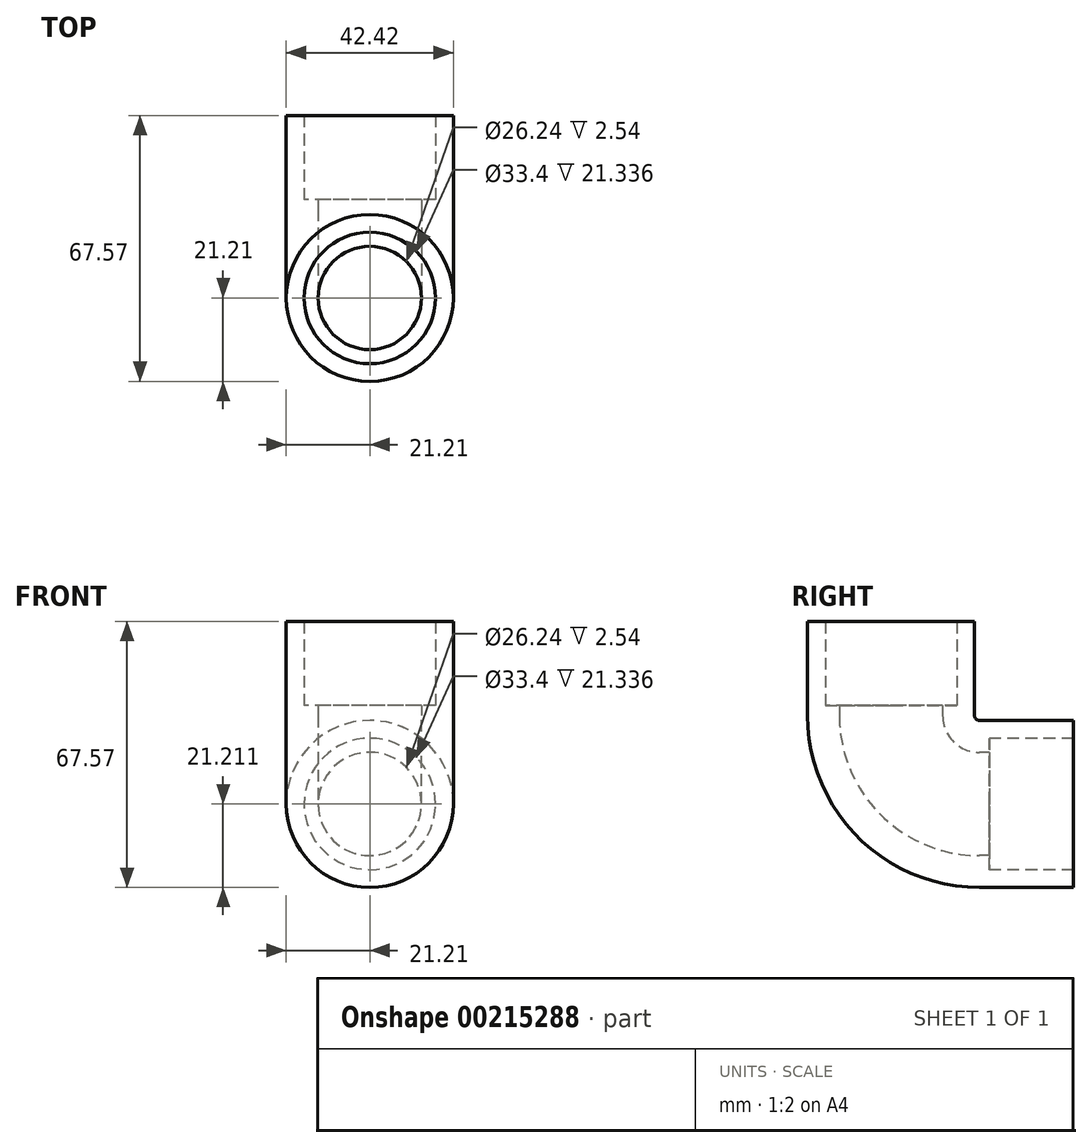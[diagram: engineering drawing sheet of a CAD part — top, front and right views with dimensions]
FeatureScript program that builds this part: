
annotation { "Feature Type Name" : "Feature", "Feature Type Description" : "" }
export const myFeature = defineFeature(function(context is Context, id is Id, definition is map)
    precondition{}
    {
        {
            var Q0;
            Q0=qCreatedBy(makeId("Top.planeOp"),FACE);
            var sketch = newSketch(context, id + "F0", { "sketchPlane" : qUnion([Q0])});
            skCircle(sketch, "E0", {"center": v(0, 0) * mm, "radius": 16.7 * mm});
            skCircle(sketch, "E1", {"center": v(0, 0) * mm, "radius": 13.12 * mm});
            skCircle(sketch, "E2", {"center": v(0, 0) * mm, "radius": 21.2 * mm});
            skSolve(sketch);
        }
        {
            var Q0;
            Q0=makeQuery(id+"F0.imprint","IMPRINT",FACE,{"disambiguationData":[TD([[makeQuery(id+"F0.imprint","IMPRINT",EDGE,{"derivedFrom":sQuery(id+"F0.wireOp",EDGE,"E0")}),1.0]])]});
            extrude(context, id + "F1", {"entities" : qUnion([Q0]), "depth" : 2.54 * mm});
        }
        {
            var Q0;
            Q0=makeQuery(id+"F0.imprint","IMPRINT",FACE,{"disambiguationData":[TD([[makeQuery(id+"F0.imprint","IMPRINT",EDGE,{"derivedFrom":sQuery(id+"F0.wireOp",EDGE,"E0")}),-1.0]])]});
            extrude(context, id + "F2", {"entities" : qUnion([Q0]), "operationType" : NewBodyOperationType.ADD, "depth" : 23.88 * mm});
        }
        {
            var Q0;
            Q0=qCreatedBy(makeId("Right.planeOp"),FACE);
            var sketch = newSketch(context, id + "F3", { "sketchPlane" : qUnion([Q0])});
            skLineSegment(sketch, "E3", {"start": v(-13.12, 0) * mm, "end": v(-21.2, 0) * mm, "construction": true});
            skLineSegment(sketch, "E4", {"start": v(21.2, 0) * mm, "end": v(13.12, 0) * mm, "construction": true});
            skCircle(sketch, "E5", {"center": v(22.48, 0) * mm, "radius": 1.27 * mm, "construction": true});
            skSolve(sketch);
        }
        {
            var Q0;
            Q0=qCreatedBy(makeId("Top.planeOp"),FACE);
            var sketch = newSketch(context, id + "F4", { "sketchPlane" : qUnion([Q0])});
            skLineSegment(sketch, "E6", {"start": v(0, 22.48) * mm, "end": v(25.4, 22.48) * mm});
            skSolve(sketch);
        }
        {
            var Q0;
            {var subQ0=sQuery(id+"F0.wireOp",EDGE,"E0");Q0=makeQuery(id+"F2.boolean.opBoolean","MERGE",FACE,{"derivedFrom":[makeQuery(id+"F1.opExtrude","CAP_FACE",FACE,{"disambiguationData":[OSD([subQ0,sQuery(id+"F0.wireOp",EDGE,"E1")])],"isStart":true}),makeQuery(id+"F2.opExtrude","CAP_FACE",FACE,{"disambiguationData":[OSD([subQ0,sQuery(id+"F0.wireOp",EDGE,"E2")])],"isStart":true})]});}
            var Q1;
            Q1=sQuery(id+"F4.wireOp",EDGE,"E6");
            revolve(context, id + "F5", {"operationType" : NewBodyOperationType.ADD, "entities" : qUnion([Q0]), "axis" : qUnion([Q1]), "revolveType" : RevolveType.ONE_DIRECTION, "angle" : 45 * degree});
        }
        {
            var Q0;
            Q0=makeQuery(id+"F1.opExtrude","SWEPT_BODY",BODY,{"disambiguationData":[OSD([sQuery(id+"F0.wireOp",EDGE,"E0"),sQuery(id+"F0.wireOp",EDGE,"E1")])]});
            var Q1;
            Q1=makeQuery(id+"F5.opRevolve","CAP_FACE",FACE,{"disambiguationData":[OSD([sQuery(id+"F0.wireOp",EDGE,"E0"),sQuery(id+"F0.wireOp",EDGE,"E1"),sQuery(id+"F0.wireOp",EDGE,"E2")])],"isStart":false});
            mirror(context, id + "F6", {"operationType" : NewBodyOperationType.ADD, "entities" : qUnion([Q0]), "mirrorPlane" : qUnion([Q1])});
        }
    });
